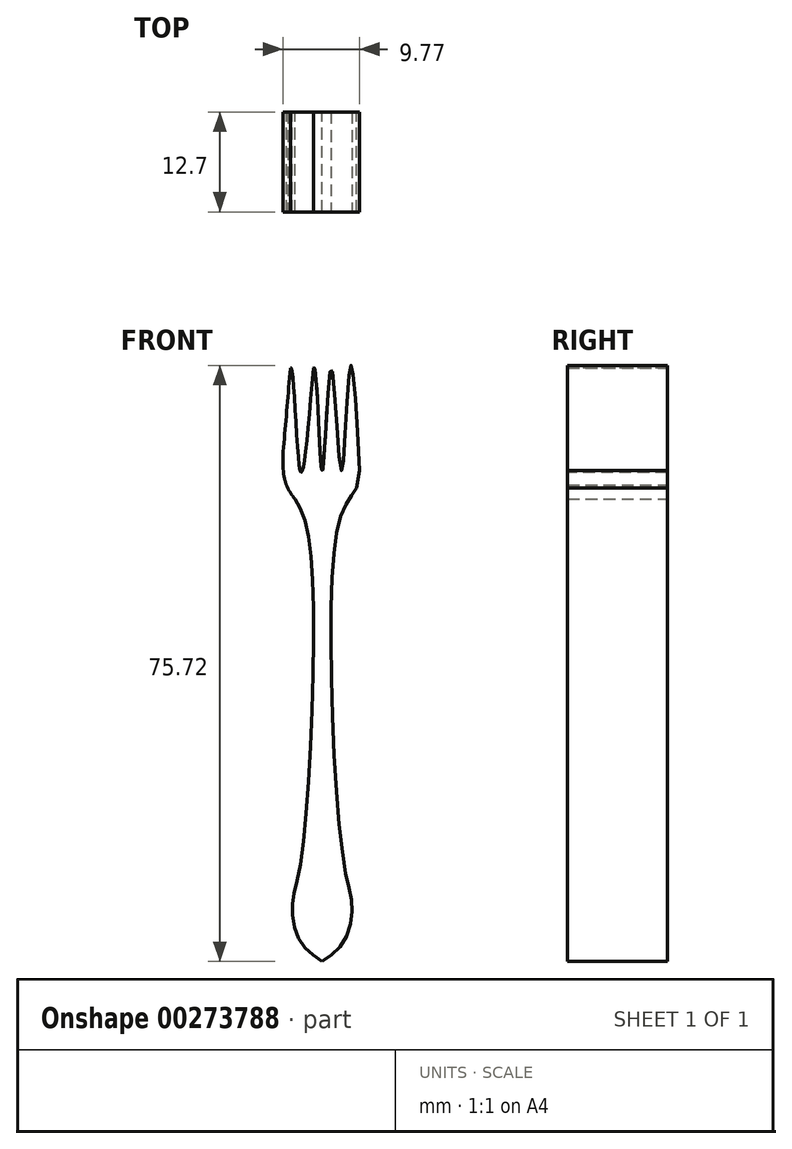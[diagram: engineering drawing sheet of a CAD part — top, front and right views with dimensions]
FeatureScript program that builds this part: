
annotation { "Feature Type Name" : "Feature", "Feature Type Description" : "" }
export const myFeature = defineFeature(function(context is Context, id is Id, definition is map)
    precondition{}
    {
        {
            var Q0;
            Q0=qCreatedBy(makeId("Front.planeOp"),FACE);
            var sketch = newSketch(context, id + "F0", { "sketchPlane" : qUnion([Q0])});
            skFitSpline(sketch, "E0", {"points": [v(-8.82, 58.16) * mm, v(-8.7, 58.16) * mm, v(-7.57, 45.15) * mm, v(-5.9, 58.16) * mm], "startDerivative": vector(2.67, 2.03) * mm, "endDerivative": vector(3.87, 46.17) * mm});
            skFitSpline(sketch, "E1", {"points": [v(-5.9, 58.16) * mm, v(-5.76, 58.16) * mm, v(-4.77, 45.15) * mm, v(-3.63, 58.16) * mm, v(-2.35, 45.15) * mm, v(-1.23, 58.16) * mm, v(0, 45.15) * mm], "startDerivative": vector(6.82, 5.99) * mm, "endDerivative": vector(6.53, -114.9) * mm});
            skPoint(sketch, "E2.0.internal.orphan", {"position": v(0, -57.64) * mm});
            skPoint(sketch, "E2.5.internal.orphan", {"position": v(-3.63, 37.83) * mm});
            skPoint(sketch, "E3.startDerivative.orphan", {"position": v(-5.9, 39.37) * mm});
            skFitSpline(sketch, "E4", {"points": [v(-3.63, 37.83) * mm, v(-9.12, 42.87) * mm, v(-9.57, 49.23) * mm, v(-8.82, 58.16) * mm], "startDerivative": vector(-20.52, 13.96) * mm, "endDerivative": vector(2.07, 25.33) * mm});
            skLineSegment(sketch, "E5", {"start": v(-4.77, 45.15) * mm, "end": v(-4.77, -17.23) * mm, "construction": true});
            skFitSpline(sketch, "E6", {"points": [v(-9.7, 44.97) * mm, v(-9.12, 42.87) * mm, v(-7.57, 40.42) * mm, v(-5.9, 27.57) * mm, v(-7.57, -4.98) * mm, v(-8.58, -10.31) * mm, v(-7.57, -14.63) * mm, v(-4.77, -17.23) * mm], "startDerivative": vector(4.84, -27.8) * mm, "endDerivative": vector(30.57, -21.1) * mm});
            skFitSpline(sketch, "E7", {"points": [v(0.16, 44.97) * mm, v(-0.42, 42.87) * mm, v(-1.97, 40.42) * mm, v(-3.65, 27.57) * mm, v(-1.97, -4.98) * mm, v(-0.96, -10.31) * mm, v(-1.97, -14.63) * mm, v(-4.77, -17.23) * mm], "startDerivative": vector(-4.84, -27.8) * mm, "endDerivative": vector(-30.57, -21.1) * mm});
            skFitSpline(sketch, "E8", {"points": [v(-0.4, 42.92) * mm, v(0, 45.15) * mm], "startDerivative": vector(0.4, 2.23) * mm, "endDerivative": vector(0.4, 2.23) * mm});
            skSolve(sketch);
        }
        {
            var Q0;
            Q0 = qSketchRegion(id + "F0", true);
            extrude(context, id + "F1", {"entities" : qUnion([Q0]), "depth" : 12.7 * mm});
        }
    });
